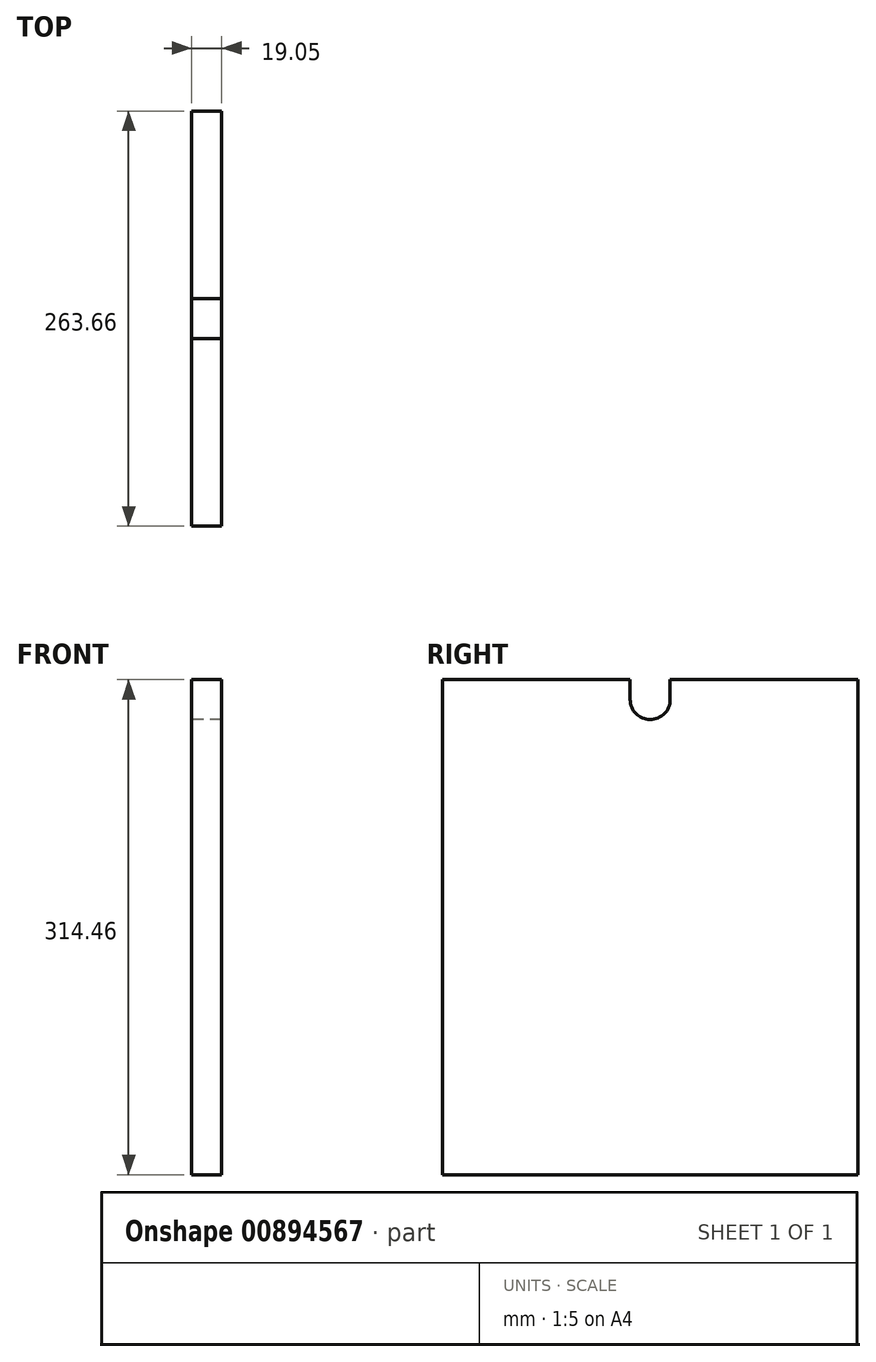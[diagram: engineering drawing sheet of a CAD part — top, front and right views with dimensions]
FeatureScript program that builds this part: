
annotation { "Feature Type Name" : "Feature", "Feature Type Description" : "" }
export const myFeature = defineFeature(function(context is Context, id is Id, definition is map)
    precondition{}
    {
        {
            var Q0;
            Q0=qCreatedBy(makeId("Right.planeOp"),FACE);
            var sketch = newSketch(context, id + "F0", { "sketchPlane" : qUnion([Q0])});
            skLineSegment(sketch, "E0.bottom", {"start": v(131.83, 157.23) * mm, "end": v(-131.83, 157.23) * mm});
            skLineSegment(sketch, "E0.top", {"start": v(131.83, -157.23) * mm, "end": v(-131.83, -157.23) * mm});
            skLineSegment(sketch, "E0.left", {"start": v(131.83, 157.23) * mm, "end": v(131.83, -157.23) * mm});
            skLineSegment(sketch, "E0.right", {"start": v(-131.83, 157.23) * mm, "end": v(-131.83, -157.23) * mm});
            skPoint(sketch, "E0.middle", {"position": v(0, 0) * mm});
            skLineSegment(sketch, "E1", {"start": v(0, 157.23) * mm, "end": v(0, 144.53) * mm});
            skCircle(sketch, "E2", {"center": v(0, 144.53) * mm, "radius": 12.7 * mm});
            skLineSegment(sketch, "E3", {"start": v(0, 144.53) * mm, "end": v(-12.7, 144.53) * mm});
            skLineSegment(sketch, "E4", {"start": v(-12.7, 144.53) * mm, "end": v(-12.7, 157.23) * mm});
            skLineSegment(sketch, "E5", {"start": v(0, 144.53) * mm, "end": v(12.7, 144.53) * mm});
            skLineSegment(sketch, "E6", {"start": v(12.7, 144.53) * mm, "end": v(12.7, 157.23) * mm});
            skSolve(sketch);
        }
        {
            var Q0;
            Q0=makeQuery(id+"F0.imprint","IMPRINT",FACE,{"disambiguationData":[TD([[makeQuery(id+"F0.imprint","IMPRINT",EDGE,{"derivedFrom":sQuery(id+"F0.wireOp",EDGE,"E0.bottom")}),1.0]])]});
            extrude(context, id + "F1", {"entities" : qUnion([Q0]), "depth" : 19.05 * mm, "offsetDistance" : 25.4 * mm});
        }
    });
